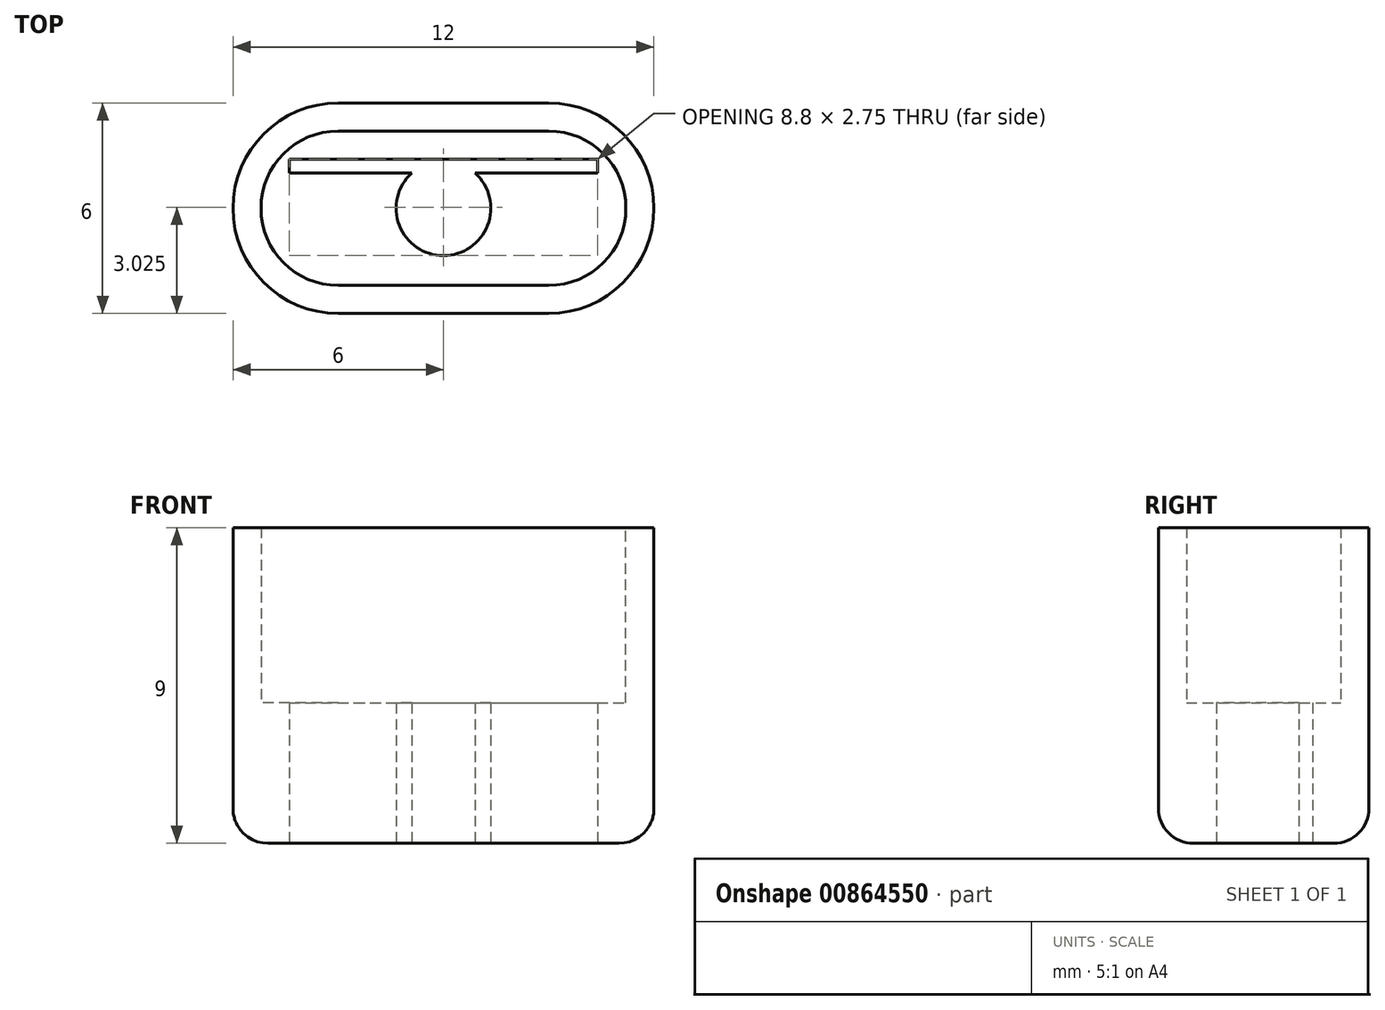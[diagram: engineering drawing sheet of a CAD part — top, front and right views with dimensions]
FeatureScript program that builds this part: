
annotation { "Feature Type Name" : "Feature", "Feature Type Description" : "" }
export const myFeature = defineFeature(function(context is Context, id is Id, definition is map)
    precondition{}
    {
        {
            var Q0;
            Q0=qCreatedBy(makeId("Top.planeOp"),FACE);
            var sketch = newSketch(context, id + "F0", { "sketchPlane" : qUnion([Q0])});
            skLineSegment(sketch, "E0.bottom", {"start": v(-6, 3) * mm, "end": v(6, 3) * mm});
            skLineSegment(sketch, "E0.top", {"start": v(-6, -3) * mm, "end": v(6, -3) * mm});
            skLineSegment(sketch, "E0.left", {"start": v(-6, 3) * mm, "end": v(-6, -3) * mm});
            skLineSegment(sketch, "E0.right", {"start": v(6, 3) * mm, "end": v(6, -3) * mm});
            skPoint(sketch, "E0.middle", {"position": v(0, 0) * mm});
            skLineSegment(sketch, "E1.bottom", {"start": v(-4, 1) * mm, "end": v(4, 1) * mm, "construction": true});
            skLineSegment(sketch, "E1.top", {"start": v(-4, -1) * mm, "end": v(4, -1) * mm, "construction": true});
            skLineSegment(sketch, "E1.left", {"start": v(-4, 1) * mm, "end": v(-4, -1) * mm, "construction": true});
            skLineSegment(sketch, "E1.right", {"start": v(4, 1) * mm, "end": v(4, -1) * mm, "construction": true});
            skLineSegment(sketch, "E2.bottom", {"start": v(-4.4, 1) * mm, "end": v(4.4, 1) * mm});
            skLineSegment(sketch, "E2.top", {"start": v(-4.4, 1.4) * mm, "end": v(4.4, 1.4) * mm});
            skLineSegment(sketch, "E2.left", {"start": v(-4.4, 1) * mm, "end": v(-4.4, 1.4) * mm});
            skLineSegment(sketch, "E2.right", {"start": v(4.4, 1) * mm, "end": v(4.4, 1.4) * mm});
            skPoint(sketch, "E3", {"position": v(0, 1.4) * mm});
            skLineSegment(sketch, "E4.bottom", {"start": v(-5.2, 2.2) * mm, "end": v(5.2, 2.2) * mm});
            skLineSegment(sketch, "E4.top", {"start": v(-5.2, -2.2) * mm, "end": v(5.2, -2.2) * mm});
            skLineSegment(sketch, "E4.left", {"start": v(-5.2, 2.2) * mm, "end": v(-5.2, -2.2) * mm});
            skLineSegment(sketch, "E4.right", {"start": v(5.2, 2.2) * mm, "end": v(5.2, -2.2) * mm});
            skCircle(sketch, "E5", {"center": v(0, 0) * mm, "radius": 1.35 * mm});
            skSolve(sketch);
        }
        {
            var Q0;
            Q0 = qSketchRegion(id + "F0", true);
            extrude(context, id + "F1", {"entities" : qUnion([Q0]), "depth" : 9 * mm, "offsetDistance" : 25 * mm});
        }
        {
            var Q0;
            Q0=makeQuery(id+"F1.opExtrude","SWEPT_EDGE",EDGE,{"disambiguationData":[OSD([sQuery(id+"F0.wireOp",EDGE,"E4.bottom"),sQuery(id+"F0.wireOp",EDGE,"E4.left")])]});
            var Q1;
            Q1=makeQuery(id+"F1.opExtrude","SWEPT_EDGE",EDGE,{"disambiguationData":[OSD([sQuery(id+"F0.wireOp",EDGE,"E4.top"),sQuery(id+"F0.wireOp",EDGE,"E4.left")])]});
            var Q2;
            Q2=makeQuery(id+"F1.opExtrude","SWEPT_EDGE",EDGE,{"disambiguationData":[OSD([sQuery(id+"F0.wireOp",EDGE,"E4.bottom"),sQuery(id+"F0.wireOp",EDGE,"E4.right")])]});
            var Q3;
            Q3=makeQuery(id+"F1.opExtrude","SWEPT_EDGE",EDGE,{"disambiguationData":[OSD([sQuery(id+"F0.wireOp",EDGE,"E4.top"),sQuery(id+"F0.wireOp",EDGE,"E4.right")])]});
            fillet(context, id + "F2", {"entities" : qUnion([Q0, Q1, Q2, Q3]), "radius" : 2.2 * mm, "tangentPropagation" : true, "allowEdgeOverflow" : false});
        }
        {
            var Q0;
            Q0=makeQuery(id+"F1.opExtrude","SWEPT_EDGE",EDGE,{"disambiguationData":[OSD([sQuery(id+"F0.wireOp",EDGE,"E0.bottom"),sQuery(id+"F0.wireOp",EDGE,"E0.left")])]});
            var Q1;
            Q1=makeQuery(id+"F1.opExtrude","SWEPT_EDGE",EDGE,{"disambiguationData":[OSD([sQuery(id+"F0.wireOp",EDGE,"E0.bottom"),sQuery(id+"F0.wireOp",EDGE,"E0.right")])]});
            var Q2;
            Q2=makeQuery(id+"F1.opExtrude","SWEPT_EDGE",EDGE,{"disambiguationData":[OSD([sQuery(id+"F0.wireOp",EDGE,"E0.top"),sQuery(id+"F0.wireOp",EDGE,"E0.left")])]});
            var Q3;
            Q3=makeQuery(id+"F1.opExtrude","SWEPT_EDGE",EDGE,{"disambiguationData":[OSD([sQuery(id+"F0.wireOp",EDGE,"E0.top"),sQuery(id+"F0.wireOp",EDGE,"E0.right")])]});
            fillet(context, id + "F3", {"entities" : qUnion([Q0, Q1, Q2, Q3]), "radius" : 3 * mm, "tangentPropagation" : true, "allowEdgeOverflow" : false});
        }
        {
            var Q0;
            Q0=makeQuery(id+"F0.imprint","IMPRINT",FACE,{"disambiguationData":[TD([[makeQuery(id+"F0.imprint","IMPRINT",EDGE,{"derivedFrom":sQuery(id+"F0.wireOp",EDGE,"E2.bottom")}),-1.0]])]});
            extrude(context, id + "F4", {"entities" : qUnion([Q0]), "operationType" : NewBodyOperationType.ADD, "depth" : 4 * mm, "offsetDistance" : 25 * mm});
        }
        {
            var Q0;
            Q0=makeQuery(id+"F4.opExtrude","SWEPT_EDGE",EDGE,{"disambiguationData":[OSD([sQuery(id+"F0.wireOp",EDGE,"E4.top"),sQuery(id+"F0.wireOp",EDGE,"E4.left")])]});
            var Q1;
            Q1=makeQuery(id+"F4.opExtrude","SWEPT_EDGE",EDGE,{"disambiguationData":[OSD([sQuery(id+"F0.wireOp",EDGE,"E4.top"),sQuery(id+"F0.wireOp",EDGE,"E4.right")])]});
            var Q2;
            Q2=makeQuery(id+"F4.opExtrude","SWEPT_EDGE",EDGE,{"disambiguationData":[OSD([sQuery(id+"F0.wireOp",EDGE,"E4.bottom"),sQuery(id+"F0.wireOp",EDGE,"E4.left")])]});
            var Q3;
            Q3=makeQuery(id+"F4.opExtrude","SWEPT_EDGE",EDGE,{"disambiguationData":[OSD([sQuery(id+"F0.wireOp",EDGE,"E4.bottom"),sQuery(id+"F0.wireOp",EDGE,"E4.right")])]});
            fillet(context, id + "F5", {"entities" : qUnion([Q0, Q1, Q2, Q3]), "radius" : 3 * mm, "tangentPropagation" : true, "allowEdgeOverflow" : false});
        }
        {
            var Q0;
            Q0=makeQuery(id+"F1.opExtrude","CAP_EDGE",EDGE,{"disambiguationData":[OSD([sQuery(id+"F0.wireOp",EDGE,"E0.top")])],"isStart":true});
            fillet(context, id + "F6", {"entities" : qUnion([Q0]), "radius" : 1 * mm, "tangentPropagation" : true, "allowEdgeOverflow" : false});
        }
    });
